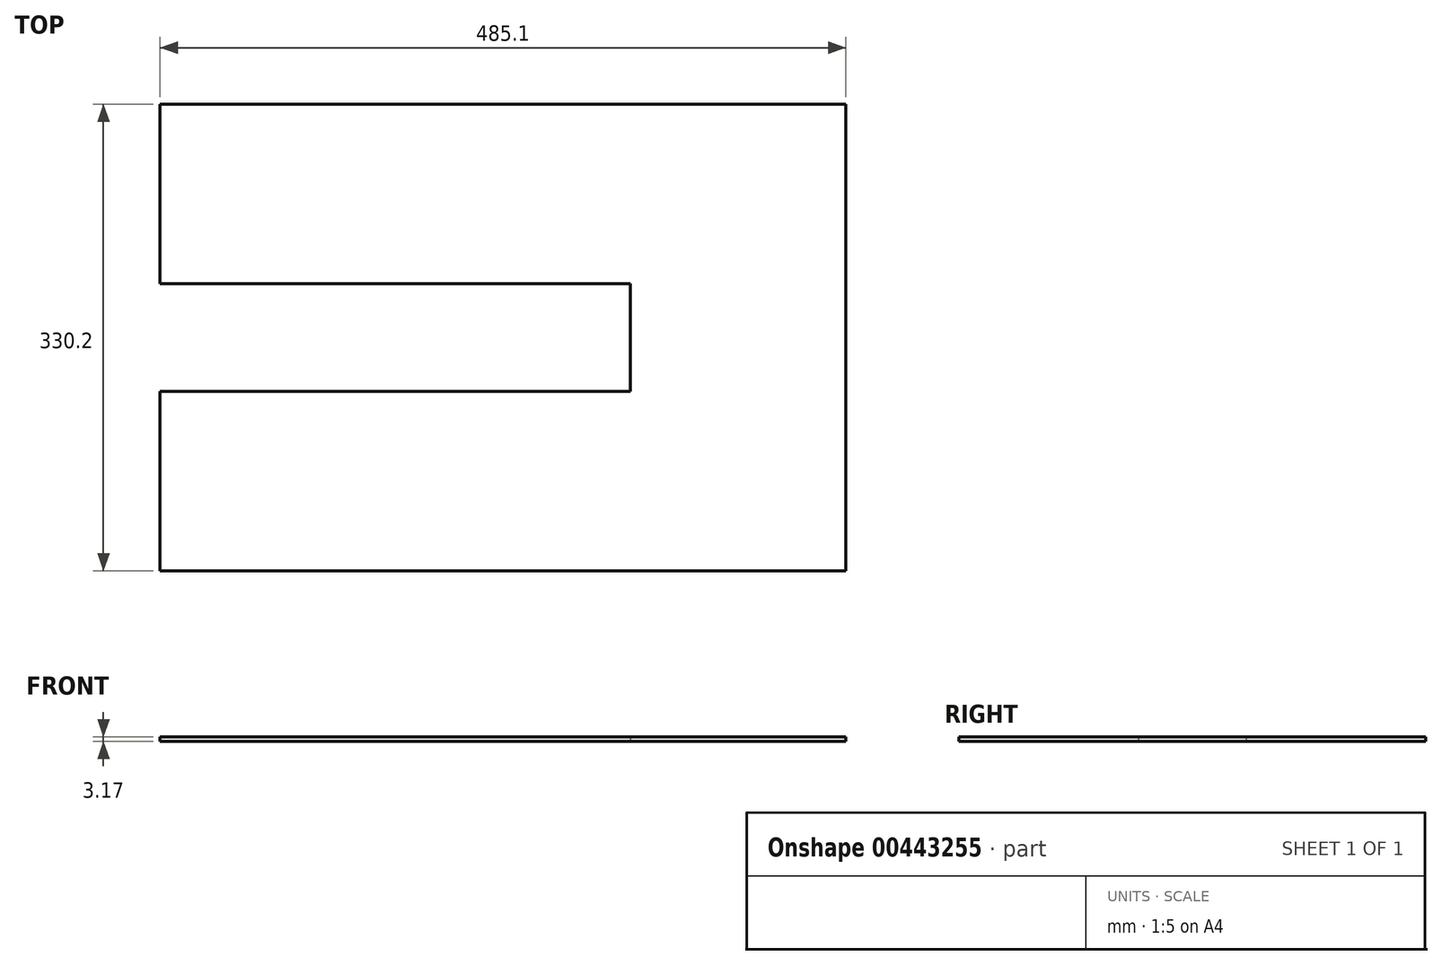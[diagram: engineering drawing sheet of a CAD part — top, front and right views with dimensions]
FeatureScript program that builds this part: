
annotation { "Feature Type Name" : "Feature", "Feature Type Description" : "" }
export const myFeature = defineFeature(function(context is Context, id is Id, definition is map)
    precondition{}
    {
        {
            var Q0;
            Q0=qCreatedBy(makeId("Top.planeOp"),FACE);
            var sketch = newSketch(context, id + "F0", { "sketchPlane" : qUnion([Q0])});
            skLineSegment(sketch, "E0.bottom", {"start": v(242.55, -165.1) * mm, "end": v(-242.55, -165.1) * mm});
            skLineSegment(sketch, "E0.top", {"start": v(242.55, 165.1) * mm, "end": v(-242.55, 165.1) * mm});
            skLineSegment(sketch, "E0.left", {"start": v(242.55, -165.1) * mm, "end": v(242.55, 165.1) * mm});
            skLineSegment(sketch, "E0.right", {"start": v(-242.55, -165.1) * mm, "end": v(-242.55, 165.1) * mm});
            skPoint(sketch, "E0.middle", {"position": v(0, 0) * mm});
            skLineSegment(sketch, "E1.bottom", {"start": v(-242.55, 38.1) * mm, "end": v(90.09, 38.1) * mm});
            skLineSegment(sketch, "E1.top", {"start": v(-242.55, -38.1) * mm, "end": v(90.09, -38.1) * mm});
            skLineSegment(sketch, "E1.left", {"start": v(-242.55, 38.1) * mm, "end": v(-242.55, -38.1) * mm});
            skLineSegment(sketch, "E1.right", {"start": v(90.09, 38.1) * mm, "end": v(90.09, -38.1) * mm});
            skSolve(sketch);
        }
        {
            var Q0;
            {var subQ1=sQuery(id+"F0.wireOp",EDGE,"E0.bottom");Q0=makeQuery(id+"F0.imprint","IMPRINT",FACE,{"disambiguationData":[TD([[makeQuery(id+"F0.imprint","IMPRINT",EDGE,{"derivedFrom":subQ1}),-1.0]])]});}
            extrude(context, id + "F1", {"entities" : qUnion([Q0]), "depth" : 3.17 * mm, "offsetDistance" : 25.4 * mm});
        }
    });
